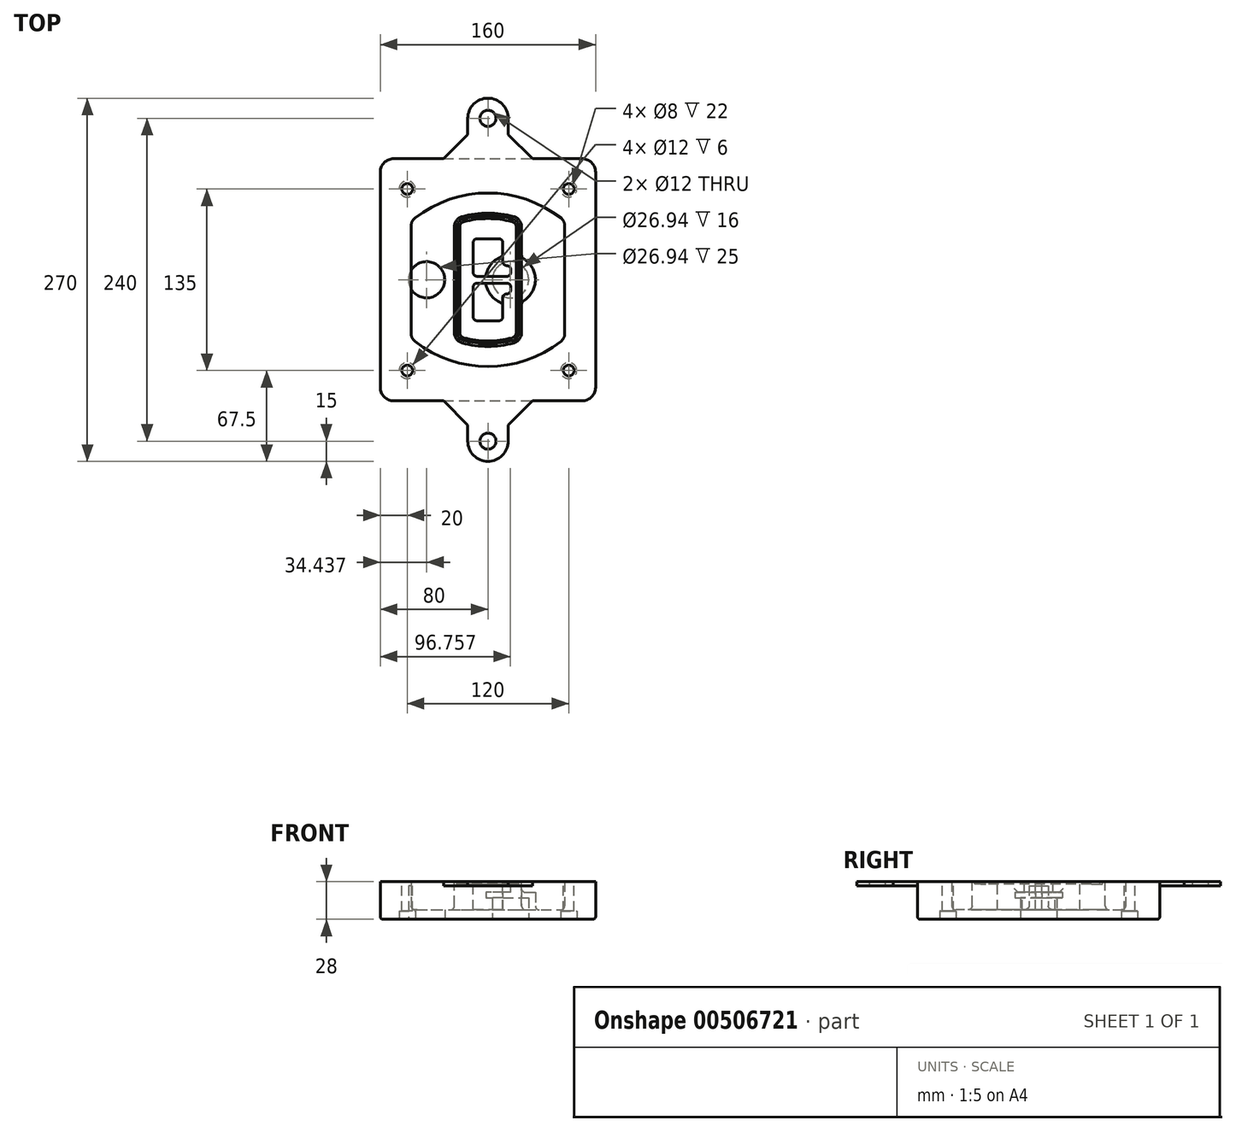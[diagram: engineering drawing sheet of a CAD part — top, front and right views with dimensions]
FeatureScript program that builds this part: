
annotation { "Feature Type Name" : "Feature", "Feature Type Description" : "" }
export const myFeature = defineFeature(function(context is Context, id is Id, definition is map)
    precondition{}
    {
        {
            var Q0;
            Q0=qCreatedBy(makeId("Top.planeOp"),FACE);
            var sketch = newSketch(context, id + "F0", { "sketchPlane" : qUnion([Q0])});
            skPoint(sketch, "E0.rect.middle", {"position": v(0, 0) * mm});
            skLineSegment(sketch, "E1.bottom", {"start": v(-70, -90) * mm, "end": v(70, -90) * mm});
            skLineSegment(sketch, "E1.top", {"start": v(-70, 90) * mm, "end": v(70, 90) * mm});
            skLineSegment(sketch, "E1.left", {"start": v(-80, -80) * mm, "end": v(-80, 80) * mm});
            skLineSegment(sketch, "E1.right", {"start": v(80, -80) * mm, "end": v(80, 80) * mm});
            skLineSegment(sketch, "E2", {"start": v(-80, 90) * mm, "end": v(80, -90) * mm, "construction": true});
            skLineSegment(sketch, "E3", {"start": v(80, 90) * mm, "end": v(-80, -90) * mm, "construction": true});
            skCircle(sketch, "E4", {"center": v(-60, 67.5) * mm, "radius": 4 * mm});
            skCircle(sketch, "E5", {"center": v(60, 67.5) * mm, "radius": 4 * mm});
            skCircle(sketch, "E6", {"center": v(60, -67.5) * mm, "radius": 4 * mm});
            skCircle(sketch, "E7", {"center": v(-60, -67.5) * mm, "radius": 4 * mm});
            skLineSegment(sketch, "E8", {"start": v(-60, 67.5) * mm, "end": v(60, 67.5) * mm, "construction": true});
            skLineSegment(sketch, "E9", {"start": v(60, 67.5) * mm, "end": v(60, -67.5) * mm, "construction": true});
            skLineSegment(sketch, "E10", {"start": v(60, -67.5) * mm, "end": v(-60, -67.5) * mm, "construction": true});
            skLineSegment(sketch, "E11", {"start": v(-60, -67.5) * mm, "end": v(-60, 67.5) * mm, "construction": true});
            skLineSegment(sketch, "E12", {"start": v(-60, 40.3) * mm, "end": v(-60, -40.3) * mm});
            skLineSegment(sketch, "E13", {"start": v(60, 40.3) * mm, "end": v(60, -40.3) * mm});
            skArc(sketch, "E14", {"start": v(56.15, 48.18) * mm, "mid": v(0, 67.5) * mm, "end": v(-56.15, 48.18) * mm});
            skArc(sketch, "E15", {"start": v(-56.15, -48.18) * mm, "mid": v(0, -67.5) * mm, "end": v(56.15, -48.18) * mm});
            skLineSegment(sketch, "E16", {"start": v(-60, 0) * mm, "end": v(60, 0) * mm, "construction": true});
            skPoint(sketch, "E17.visualSharp", {"position": v(-60, -45) * mm});
            skArc(sketch, "E17.filletArc", {"start": v(-60, -40.3) * mm, "mid": v(-58.99, -44.68) * mm, "end": v(-56.15, -48.18) * mm});
            skPoint(sketch, "E18.visualSharp", {"position": v(-60, 45) * mm});
            skArc(sketch, "E18.filletArc", {"start": v(-56.15, 48.18) * mm, "mid": v(-58.99, 44.68) * mm, "end": v(-60, 40.3) * mm});
            skPoint(sketch, "E19.visualSharp", {"position": v(60, 45) * mm});
            skArc(sketch, "E19.filletArc", {"start": v(60, 40.3) * mm, "mid": v(58.99, 44.68) * mm, "end": v(56.15, 48.18) * mm});
            skPoint(sketch, "E20.visualSharp", {"position": v(60, -45) * mm});
            skArc(sketch, "E20.filletArc", {"start": v(56.15, -48.18) * mm, "mid": v(58.99, -44.68) * mm, "end": v(60, -40.3) * mm});
            skPoint(sketch, "E21.visualSharp", {"position": v(-80, 90) * mm});
            skArc(sketch, "E21.filletArc", {"start": v(-70, 90) * mm, "mid": v(-77.07, 87.07) * mm, "end": v(-80, 80) * mm});
            skPoint(sketch, "E22.visualSharp", {"position": v(80, 90) * mm});
            skArc(sketch, "E22.filletArc", {"start": v(80, 80) * mm, "mid": v(77.07, 87.07) * mm, "end": v(70, 90) * mm});
            skPoint(sketch, "E23.visualSharp", {"position": v(80, -90) * mm});
            skArc(sketch, "E23.filletArc", {"start": v(70, -90) * mm, "mid": v(77.07, -87.07) * mm, "end": v(80, -80) * mm});
            skPoint(sketch, "E24.visualSharp", {"position": v(-80, -90) * mm});
            skArc(sketch, "E24.filletArc", {"start": v(-80, -80) * mm, "mid": v(-77.07, -87.07) * mm, "end": v(-70, -90) * mm});
            skArc(sketch, "E25.0", {"start": v(57, 40.3) * mm, "mid": v(56.3, 43.36) * mm, "end": v(54.3, 45.81) * mm});
            skLineSegment(sketch, "E25.1", {"start": v(57, 40.3) * mm, "end": v(57, -40.3) * mm});
            skArc(sketch, "E25.2", {"start": v(54.3, -45.81) * mm, "mid": v(56.3, -43.36) * mm, "end": v(57, -40.3) * mm});
            skArc(sketch, "E25.3", {"start": v(-54.3, -45.81) * mm, "mid": v(0, -64.5) * mm, "end": v(54.3, -45.81) * mm});
            skArc(sketch, "E25.4", {"start": v(-57, -40.3) * mm, "mid": v(-56.3, -43.36) * mm, "end": v(-54.3, -45.81) * mm});
            skArc(sketch, "E25.5", {"start": v(54.3, 45.81) * mm, "mid": v(0, 64.5) * mm, "end": v(-54.3, 45.81) * mm});
            skLineSegment(sketch, "E25.6", {"start": v(-57, 40.3) * mm, "end": v(-57, -40.3) * mm});
            skArc(sketch, "E25.7", {"start": v(-54.3, 45.81) * mm, "mid": v(-56.3, 43.36) * mm, "end": v(-57, 40.3) * mm});
            skArc(sketch, "E26.0", {"start": v(-58.62, 51.33) * mm, "mid": v(-62.58, 46.43) * mm, "end": v(-64, 40.3) * mm});
            skArc(sketch, "E26.1", {"start": v(58.62, 51.33) * mm, "mid": v(0, 71.5) * mm, "end": v(-58.62, 51.33) * mm});
            skArc(sketch, "E26.2", {"start": v(64, 40.3) * mm, "mid": v(62.58, 46.43) * mm, "end": v(58.62, 51.33) * mm});
            skLineSegment(sketch, "E26.3", {"start": v(64, 40.3) * mm, "end": v(64, -40.3) * mm});
            skArc(sketch, "E26.4", {"start": v(58.62, -51.33) * mm, "mid": v(62.58, -46.43) * mm, "end": v(64, -40.3) * mm});
            skLineSegment(sketch, "E26.5", {"start": v(-64, 40.3) * mm, "end": v(-64, -40.3) * mm});
            skArc(sketch, "E26.6", {"start": v(-58.62, -51.33) * mm, "mid": v(0, -71.5) * mm, "end": v(58.62, -51.33) * mm});
            skArc(sketch, "E26.7", {"start": v(-64, -40.3) * mm, "mid": v(-62.58, -46.43) * mm, "end": v(-58.62, -51.33) * mm});
            skSolve(sketch);
        }
        {
            var Q0;
            Q0=makeQuery(id+"F0.imprint","IMPRINT",FACE,{"disambiguationData":[TD([[makeQuery(id+"F0.imprint","IMPRINT",EDGE,{"derivedFrom":sQuery(id+"F0.wireOp",EDGE,"E1.bottom")}),1.0]])]});
            var Q1;
            Q1=makeQuery(id+"F0.imprint","IMPRINT",FACE,{"disambiguationData":[TD([[makeQuery(id+"F0.imprint","IMPRINT",EDGE,{"derivedFrom":sQuery(id+"F0.wireOp",EDGE,"E12")}),1.0]])]});
            var Q2;
            Q2=makeQuery(id+"F0.imprint","IMPRINT",FACE,{"disambiguationData":[TD([[makeQuery(id+"F0.imprint","IMPRINT",EDGE,{"derivedFrom":sQuery(id+"F0.wireOp",EDGE,"E25.0")}),1.0]])]});
            var Q3;
            Q3=makeQuery(id+"F0.imprint","IMPRINT",FACE,{"disambiguationData":[TD([[makeQuery(id+"F0.imprint","IMPRINT",EDGE,{"derivedFrom":sQuery(id+"F0.wireOp",EDGE,"E12")}),-1.0]])]});
            extrude(context, id + "F1", {"entities" : qUnion([Q0, Q1, Q2, Q3]), "oppositeDirection" : true, "depth" : 25 * mm});
        }
        {
            var Q0;
            Q0=makeQuery(id+"F0.imprint","IMPRINT",FACE,{"disambiguationData":[TD([[makeQuery(id+"F0.imprint","IMPRINT",EDGE,{"derivedFrom":sQuery(id+"F0.wireOp",EDGE,"E12")}),1.0]])]});
            extrude(context, id + "F2", {"entities" : qUnion([Q0]), "operationType" : NewBodyOperationType.ADD, "depth" : 3 * mm});
        }
        {
            var Q0;
            Q0=makeQuery(id+"F0.imprint","IMPRINT",FACE,{"disambiguationData":[TD([[makeQuery(id+"F0.imprint","IMPRINT",EDGE,{"derivedFrom":sQuery(id+"F0.wireOp",EDGE,"E25.0")}),1.0]])]});
            extrude(context, id + "F3", {"entities" : qUnion([Q0]), "operationType" : NewBodyOperationType.REMOVE, "oppositeDirection" : true, "depth" : 18 * mm});
        }
        {
            var Q0;
            Q0=makeQuery(id+"F2.opExtrude","CAP_FACE",FACE,{"disambiguationData":[OSD([sQuery(id+"F0.wireOp",EDGE,"E12"),sQuery(id+"F0.wireOp",EDGE,"E13"),sQuery(id+"F0.wireOp",EDGE,"E14"),sQuery(id+"F0.wireOp",EDGE,"E15"),sQuery(id+"F0.wireOp",EDGE,"E17.filletArc"),sQuery(id+"F0.wireOp",EDGE,"E18.filletArc"),sQuery(id+"F0.wireOp",EDGE,"E19.filletArc"),sQuery(id+"F0.wireOp",EDGE,"E20.filletArc"),sQuery(id+"F0.wireOp",EDGE,"E25.0"),sQuery(id+"F0.wireOp",EDGE,"E25.1"),sQuery(id+"F0.wireOp",EDGE,"E25.2"),sQuery(id+"F0.wireOp",EDGE,"E25.3"),sQuery(id+"F0.wireOp",EDGE,"E25.4"),sQuery(id+"F0.wireOp",EDGE,"E25.5"),sQuery(id+"F0.wireOp",EDGE,"E25.6"),sQuery(id+"F0.wireOp",EDGE,"E25.7")])],"isStart":false});
            var sketch = newSketch(context, id + "F4", { "sketchPlane" : qUnion([Q0])});
            skArc(sketch, "E27.0", {"start": v(-19.08, -46.97) * mm, "mid": v(0, -49.5) * mm, "end": v(19.08, -46.97) * mm});
            skArc(sketch, "E28.0", {"start": v(19.08, 46.97) * mm, "mid": v(0, 49.5) * mm, "end": v(-19.08, 46.97) * mm});
            skLineSegment(sketch, "E29", {"start": v(-25, 39.25) * mm, "end": v(-25, -39.25) * mm});
            skLineSegment(sketch, "E30", {"start": v(25, 39.25) * mm, "end": v(25, -39.25) * mm});
            skLineSegment(sketch, "E31", {"start": v(-25, 45.1) * mm, "end": v(25, 45.1) * mm, "construction": true});
            skLineSegment(sketch, "E32", {"start": v(-25, -45.1) * mm, "end": v(25, -45.1) * mm, "construction": true});
            skPoint(sketch, "E33.visualSharp", {"position": v(-25, 45.1) * mm});
            skArc(sketch, "E33.filletArc", {"start": v(-19.08, 46.97) * mm, "mid": v(-23.35, 44.11) * mm, "end": v(-25, 39.25) * mm});
            skPoint(sketch, "E34.visualSharp", {"position": v(25, 45.1) * mm});
            skArc(sketch, "E34.filletArc", {"start": v(25, 39.25) * mm, "mid": v(23.35, 44.11) * mm, "end": v(19.08, 46.97) * mm});
            skPoint(sketch, "E35.visualSharp", {"position": v(25, -45.1) * mm});
            skArc(sketch, "E35.filletArc", {"start": v(19.08, -46.97) * mm, "mid": v(23.35, -44.11) * mm, "end": v(25, -39.25) * mm});
            skPoint(sketch, "E36.visualSharp", {"position": v(-25, -45.1) * mm});
            skArc(sketch, "E36.filletArc", {"start": v(-25, -39.25) * mm, "mid": v(-23.35, -44.11) * mm, "end": v(-19.08, -46.97) * mm});
            skArc(sketch, "E37.0", {"start": v(54.3, 45.81) * mm, "mid": v(0, 64.5) * mm, "end": v(-54.3, 45.81) * mm});
            skArc(sketch, "E37.1", {"start": v(-54.3, 45.81) * mm, "mid": v(-56.3, 43.36) * mm, "end": v(-57, 40.3) * mm});
            skLineSegment(sketch, "E37.2", {"start": v(-57, 40.3) * mm, "end": v(-57, -40.3) * mm});
            skArc(sketch, "E37.3", {"start": v(-57, -40.3) * mm, "mid": v(-56.3, -43.36) * mm, "end": v(-54.3, -45.81) * mm});
            skArc(sketch, "E37.4", {"start": v(-54.3, -45.81) * mm, "mid": v(0, -64.5) * mm, "end": v(54.3, -45.81) * mm});
            skArc(sketch, "E37.5", {"start": v(54.3, -45.81) * mm, "mid": v(56.3, -43.36) * mm, "end": v(57, -40.3) * mm});
            skLineSegment(sketch, "E37.6", {"start": v(57, 40.3) * mm, "end": v(57, -40.3) * mm});
            skArc(sketch, "E37.7", {"start": v(57, 40.3) * mm, "mid": v(56.3, 43.36) * mm, "end": v(54.3, 45.81) * mm});
            skLineSegment(sketch, "E38.0", {"start": v(23, 39.25) * mm, "end": v(23, -39.25) * mm});
            skArc(sketch, "E38.1", {"start": v(18.56, -45.04) * mm, "mid": v(21.76, -42.9) * mm, "end": v(23, -39.25) * mm});
            skArc(sketch, "E38.2", {"start": v(-18.56, -45.04) * mm, "mid": v(0, -47.5) * mm, "end": v(18.56, -45.04) * mm});
            skArc(sketch, "E38.3", {"start": v(-23, -39.25) * mm, "mid": v(-21.76, -42.9) * mm, "end": v(-18.56, -45.04) * mm});
            skLineSegment(sketch, "E38.4", {"start": v(-23, 39.25) * mm, "end": v(-23, -39.25) * mm});
            skArc(sketch, "E38.5", {"start": v(23, 39.25) * mm, "mid": v(21.76, 42.9) * mm, "end": v(18.56, 45.04) * mm});
            skArc(sketch, "E38.6", {"start": v(-18.56, 45.04) * mm, "mid": v(-21.76, 42.9) * mm, "end": v(-23, 39.25) * mm});
            skArc(sketch, "E38.7", {"start": v(18.56, 45.04) * mm, "mid": v(0, 47.5) * mm, "end": v(-18.56, 45.04) * mm});
            skArc(sketch, "E39.0", {"start": v(21, 39.25) * mm, "mid": v(20.18, 41.68) * mm, "end": v(18.04, 43.1) * mm});
            skLineSegment(sketch, "E39.1", {"start": v(21, 39.25) * mm, "end": v(21, -39.25) * mm});
            skArc(sketch, "E39.2", {"start": v(18.04, -43.1) * mm, "mid": v(20.18, -41.68) * mm, "end": v(21, -39.25) * mm});
            skArc(sketch, "E39.3", {"start": v(-18.04, -43.1) * mm, "mid": v(0, -45.5) * mm, "end": v(18.04, -43.1) * mm});
            skArc(sketch, "E39.4", {"start": v(-21, -39.25) * mm, "mid": v(-20.18, -41.68) * mm, "end": v(-18.04, -43.1) * mm});
            skArc(sketch, "E39.5", {"start": v(18.04, 43.1) * mm, "mid": v(0, 45.5) * mm, "end": v(-18.04, 43.1) * mm});
            skLineSegment(sketch, "E39.6", {"start": v(-21, 39.25) * mm, "end": v(-21, -39.25) * mm});
            skArc(sketch, "E39.7", {"start": v(-18.04, 43.1) * mm, "mid": v(-20.18, 41.68) * mm, "end": v(-21, 39.25) * mm});
            skLineSegment(sketch, "E40", {"start": v(-25, 0) * mm, "end": v(25, 0) * mm, "construction": true});
            skLineSegment(sketch, "E41", {"start": v(-11, 5.5) * mm, "end": v(-11, 27.5) * mm});
            skLineSegment(sketch, "E42", {"start": v(-8, 30.5) * mm, "end": v(8, 30.5) * mm});
            skLineSegment(sketch, "E43", {"start": v(11, 27.5) * mm, "end": v(11, 13.5) * mm});
            skLineSegment(sketch, "E44", {"start": v(14, 10.5) * mm, "end": v(14, 10.5) * mm});
            skLineSegment(sketch, "E45", {"start": v(17, 7.5) * mm, "end": v(17, 5.5) * mm});
            skLineSegment(sketch, "E46", {"start": v(14, 2.5) * mm, "end": v(-8, 2.5) * mm});
            skPoint(sketch, "E47.visualSharp", {"position": v(-11, 30.5) * mm});
            skArc(sketch, "E47.filletArc", {"start": v(-8, 30.5) * mm, "mid": v(-10.12, 29.62) * mm, "end": v(-11, 27.5) * mm});
            skPoint(sketch, "E48.visualSharp", {"position": v(11, 30.5) * mm});
            skArc(sketch, "E48.filletArc", {"start": v(11, 27.5) * mm, "mid": v(10.12, 29.62) * mm, "end": v(8, 30.5) * mm});
            skPoint(sketch, "E49.visualSharp", {"position": v(11, 10.5) * mm});
            skArc(sketch, "E49.filletArc", {"start": v(11, 13.5) * mm, "mid": v(11.88, 11.38) * mm, "end": v(14, 10.5) * mm});
            skPoint(sketch, "E50.visualSharp", {"position": v(17, 10.5) * mm});
            skArc(sketch, "E50.filletArc", {"start": v(17, 7.5) * mm, "mid": v(16.12, 9.62) * mm, "end": v(14, 10.5) * mm});
            skPoint(sketch, "E51.visualSharp", {"position": v(17, 2.5) * mm});
            skArc(sketch, "E51.filletArc", {"start": v(14, 2.5) * mm, "mid": v(16.12, 3.38) * mm, "end": v(17, 5.5) * mm});
            skPoint(sketch, "E52.visualSharp", {"position": v(-11, 2.5) * mm});
            skArc(sketch, "E52.filletArc", {"start": v(-11, 5.5) * mm, "mid": v(-10.12, 3.38) * mm, "end": v(-8, 2.5) * mm});
            skLineSegment(sketch, "E53.0.MirrorCS", {"start": v(14, -2.5) * mm, "end": v(-8, -2.5) * mm});
            skArc(sketch, "E54.0.MirrorCS", {"start": v(-11, -5.5) * mm, "mid": v(-10.12, -3.38) * mm, "end": v(-8, -2.5) * mm});
            skLineSegment(sketch, "E55.0.MirrorCS", {"start": v(-11, -5.5) * mm, "end": v(-11, -27.5) * mm});
            skArc(sketch, "E56.0.MirrorCS", {"start": v(-8, -30.5) * mm, "mid": v(-10.12, -29.62) * mm, "end": v(-11, -27.5) * mm});
            skLineSegment(sketch, "E57.0.MirrorCS", {"start": v(-8, -30.5) * mm, "end": v(8, -30.5) * mm});
            skArc(sketch, "E58.0.MirrorCS", {"start": v(11, -27.5) * mm, "mid": v(10.12, -29.62) * mm, "end": v(8, -30.5) * mm});
            skLineSegment(sketch, "E59.0.MirrorCS", {"start": v(11, -27.5) * mm, "end": v(11, -13.5) * mm});
            skArc(sketch, "E60.0.MirrorCS", {"start": v(11, -13.5) * mm, "mid": v(11.88, -11.38) * mm, "end": v(14, -10.5) * mm});
            skArc(sketch, "E61.0.MirrorCS", {"start": v(17, -7.5) * mm, "mid": v(16.12, -9.62) * mm, "end": v(14, -10.5) * mm});
            skLineSegment(sketch, "E62.0.MirrorCS", {"start": v(17, -7.5) * mm, "end": v(17, -5.5) * mm});
            skArc(sketch, "E63.0.MirrorCS", {"start": v(14, -2.5) * mm, "mid": v(16.12, -3.38) * mm, "end": v(17, -5.5) * mm});
            skSolve(sketch);
        }
        {
            var Q0;
            Q0=makeQuery(id+"F4.imprint","IMPRINT",FACE,{"disambiguationData":[TD([[makeQuery(id+"F4.imprint","IMPRINT",EDGE,{"derivedFrom":sQuery(id+"F4.wireOp",EDGE,"E27.0")}),1.0]])]});
            var Q1;
            Q1=makeQuery(id+"F4.imprint","IMPRINT",FACE,{"disambiguationData":[TD([[makeQuery(id+"F4.imprint","IMPRINT",EDGE,{"derivedFrom":sQuery(id+"F4.wireOp",EDGE,"E38.0")}),-1.0]])]});
            var Q2;
            Q2=makeQuery(id+"F4.imprint","IMPRINT",FACE,{"disambiguationData":[TD([[makeQuery(id+"F4.imprint","IMPRINT",EDGE,{"derivedFrom":sQuery(id+"F4.wireOp",EDGE,"E39.0")}),1.0]])]});
            extrude(context, id + "F5", {"entities" : qUnion([Q0, Q1, Q2]), "operationType" : NewBodyOperationType.ADD, "endBound" : BoundingType.UP_TO_NEXT, "oppositeDirection" : true, "depth" : 25 * mm});
        }
        {
            var Q0;
            Q0=makeQuery(id+"F4.imprint","IMPRINT",FACE,{"disambiguationData":[TD([[makeQuery(id+"F4.imprint","IMPRINT",EDGE,{"derivedFrom":sQuery(id+"F4.wireOp",EDGE,"E38.0")}),-1.0]])]});
            extrude(context, id + "F6", {"entities" : qUnion([Q0]), "operationType" : NewBodyOperationType.REMOVE, "oppositeDirection" : true, "depth" : 2 * mm});
        }
        {
            var Q0;
            Q0=makeQuery(id+"F1.opExtrude","CAP_FACE",FACE,{"disambiguationData":[OSD([sQuery(id+"F0.wireOp",EDGE,"E1.bottom"),sQuery(id+"F0.wireOp",EDGE,"E1.top"),sQuery(id+"F0.wireOp",EDGE,"E1.left"),sQuery(id+"F0.wireOp",EDGE,"E1.right"),sQuery(id+"F0.wireOp",EDGE,"E4"),sQuery(id+"F0.wireOp",EDGE,"E5"),sQuery(id+"F0.wireOp",EDGE,"E6"),sQuery(id+"F0.wireOp",EDGE,"E7"),sQuery(id+"F0.wireOp",EDGE,"E21.filletArc"),sQuery(id+"F0.wireOp",EDGE,"E22.filletArc"),sQuery(id+"F0.wireOp",EDGE,"E23.filletArc"),sQuery(id+"F0.wireOp",EDGE,"E24.filletArc")])],"isStart":false});
            var sketch = newSketch(context, id + "F7", { "sketchPlane" : qUnion([Q0])});
            skCircle(sketch, "E64", {"center": v(16.76, 0) * mm, "radius": 13.47 * mm});
            skCircle(sketch, "E65", {"center": v(-45.56, 0) * mm, "radius": 13.47 * mm});
            skLineSegment(sketch, "E66", {"start": v(80, 0) * mm, "end": v(-80, 0) * mm});
            skCircle(sketch, "E67", {"center": v(16.76, 0) * mm, "radius": 18.47 * mm});
            skCircle(sketch, "E68", {"center": v(60, -67.5) * mm, "radius": 6 * mm});
            skCircle(sketch, "E69", {"center": v(-60, -67.5) * mm, "radius": 6 * mm});
            skCircle(sketch, "E70", {"center": v(-60, 67.5) * mm, "radius": 6 * mm});
            skCircle(sketch, "E71", {"center": v(60, 67.5) * mm, "radius": 6 * mm});
            skSolve(sketch);
        }
        {
            var Q0;
            {var subQ1=sQuery(id+"F7.wireOp",EDGE,"E66");var subQ4=sQuery(id+"F7.wireOp",EDGE,"E64");var subQ6=makeQuery(id+"F7.imprint","INTERSECT",VERTEX,{"disambiguationData":[OD(0.0)],"derivedFrom":[subQ4,subQ1]});Q0=makeQuery(id+"F7.imprint","IMPRINT",FACE,{"disambiguationData":[TD([[makeQuery(id+"F7.imprint","IMPRINT",EDGE,{"disambiguationData":[TD([[subQ6,-1.0]])],"derivedFrom":subQ4}),-1.0]])]});}
            var Q1;
            {var subQ0=sQuery(id+"F7.wireOp",EDGE,"E66");var subQ1=sQuery(id+"F7.wireOp",EDGE,"E64");var subQ3=makeQuery(id+"F7.imprint","INTERSECT",VERTEX,{"disambiguationData":[OD(0.0)],"derivedFrom":[subQ1,subQ0]});Q1=makeQuery(id+"F7.imprint","IMPRINT",FACE,{"disambiguationData":[TD([[makeQuery(id+"F7.imprint","IMPRINT",EDGE,{"disambiguationData":[TD([[subQ3,-1.0]])],"derivedFrom":subQ1}),1.0]])]});}
            var Q2;
            {var subQ0=sQuery(id+"F7.wireOp",EDGE,"E66");var subQ1=sQuery(id+"F7.wireOp",EDGE,"E64");var subQ3=makeQuery(id+"F7.imprint","INTERSECT",VERTEX,{"disambiguationData":[OD(0.0)],"derivedFrom":[subQ1,subQ0]});Q2=makeQuery(id+"F7.imprint","IMPRINT",FACE,{"disambiguationData":[TD([[makeQuery(id+"F7.imprint","IMPRINT",EDGE,{"disambiguationData":[TD([[subQ3,1.0]])],"derivedFrom":subQ1}),1.0]])]});}
            var Q3;
            {var subQ1=sQuery(id+"F7.wireOp",EDGE,"E66");var subQ4=sQuery(id+"F7.wireOp",EDGE,"E64");var subQ6=makeQuery(id+"F7.imprint","INTERSECT",VERTEX,{"disambiguationData":[OD(0.0)],"derivedFrom":[subQ4,subQ1]});Q3=makeQuery(id+"F7.imprint","IMPRINT",FACE,{"disambiguationData":[TD([[makeQuery(id+"F7.imprint","IMPRINT",EDGE,{"disambiguationData":[TD([[subQ6,1.0]])],"derivedFrom":subQ4}),-1.0]])]});}
            extrude(context, id + "F8", {"entities" : qUnion([Q0, Q1, Q2, Q3]), "operationType" : NewBodyOperationType.ADD, "oppositeDirection" : true, "depth" : 20 * mm});
        }
        {
            var Q0;
            {var subQ0=sQuery(id+"F7.wireOp",EDGE,"E66");var subQ1=sQuery(id+"F7.wireOp",EDGE,"E64");var subQ3=makeQuery(id+"F7.imprint","INTERSECT",VERTEX,{"disambiguationData":[OD(0.0)],"derivedFrom":[subQ1,subQ0]});Q0=makeQuery(id+"F7.imprint","IMPRINT",FACE,{"disambiguationData":[TD([[makeQuery(id+"F7.imprint","IMPRINT",EDGE,{"disambiguationData":[TD([[subQ3,-1.0]])],"derivedFrom":subQ1}),1.0]])]});}
            var Q1;
            {var subQ0=sQuery(id+"F7.wireOp",EDGE,"E66");var subQ1=sQuery(id+"F7.wireOp",EDGE,"E64");var subQ3=makeQuery(id+"F7.imprint","INTERSECT",VERTEX,{"disambiguationData":[OD(0.0)],"derivedFrom":[subQ1,subQ0]});Q1=makeQuery(id+"F7.imprint","IMPRINT",FACE,{"disambiguationData":[TD([[makeQuery(id+"F7.imprint","IMPRINT",EDGE,{"disambiguationData":[TD([[subQ3,1.0]])],"derivedFrom":subQ1}),1.0]])]});}
            extrude(context, id + "F9", {"entities" : qUnion([Q0, Q1]), "operationType" : NewBodyOperationType.REMOVE, "oppositeDirection" : true, "depth" : 16 * mm});
        }
        {
            var Q0;
            {var subQ0=sQuery(id+"F7.wireOp",EDGE,"E66");var subQ1=sQuery(id+"F7.wireOp",EDGE,"E65");var subQ3=makeQuery(id+"F7.imprint","INTERSECT",VERTEX,{"disambiguationData":[OD(0.0)],"derivedFrom":[subQ1,subQ0]});Q0=makeQuery(id+"F7.imprint","IMPRINT",FACE,{"disambiguationData":[TD([[makeQuery(id+"F7.imprint","IMPRINT",EDGE,{"disambiguationData":[TD([[subQ3,-1.0]])],"derivedFrom":subQ1}),1.0]])]});}
            var Q1;
            {var subQ0=sQuery(id+"F7.wireOp",EDGE,"E66");var subQ1=sQuery(id+"F7.wireOp",EDGE,"E65");var subQ3=makeQuery(id+"F7.imprint","INTERSECT",VERTEX,{"disambiguationData":[OD(0.0)],"derivedFrom":[subQ1,subQ0]});Q1=makeQuery(id+"F7.imprint","IMPRINT",FACE,{"disambiguationData":[TD([[makeQuery(id+"F7.imprint","IMPRINT",EDGE,{"disambiguationData":[TD([[subQ3,1.0]])],"derivedFrom":subQ1}),1.0]])]});}
            extrude(context, id + "F10", {"entities" : qUnion([Q0, Q1]), "operationType" : NewBodyOperationType.REMOVE, "oppositeDirection" : true, "depth" : 25 * mm});
        }
        {
            var Q0;
            Q0=makeQuery(id+"F7.imprint","IMPRINT",FACE,{"disambiguationData":[TD([[makeQuery(id+"F7.imprint","IMPRINT",EDGE,{"derivedFrom":sQuery(id+"F7.wireOp",EDGE,"E68")}),1.0]])]});
            var Q1;
            Q1=makeQuery(id+"F7.imprint","IMPRINT",FACE,{"disambiguationData":[TD([[makeQuery(id+"F7.imprint","IMPRINT",EDGE,{"derivedFrom":makeQuery(id+"F1.opExtrude","CAP_EDGE",EDGE,{"disambiguationData":[OSD([sQuery(id+"F0.wireOp",EDGE,"E5")])],"isStart":false})}),-1.0]])]});
            var Q2;
            Q2=makeQuery(id+"F7.imprint","IMPRINT",FACE,{"disambiguationData":[TD([[makeQuery(id+"F7.imprint","IMPRINT",EDGE,{"derivedFrom":sQuery(id+"F7.wireOp",EDGE,"E69")}),1.0]])]});
            var Q3;
            Q3=makeQuery(id+"F7.imprint","IMPRINT",FACE,{"disambiguationData":[TD([[makeQuery(id+"F7.imprint","IMPRINT",EDGE,{"derivedFrom":makeQuery(id+"F1.opExtrude","CAP_EDGE",EDGE,{"disambiguationData":[OSD([sQuery(id+"F0.wireOp",EDGE,"E4")])],"isStart":false})}),-1.0]])]});
            var Q4;
            Q4=makeQuery(id+"F7.imprint","IMPRINT",FACE,{"disambiguationData":[TD([[makeQuery(id+"F7.imprint","IMPRINT",EDGE,{"derivedFrom":sQuery(id+"F7.wireOp",EDGE,"E70")}),1.0]])]});
            var Q5;
            Q5=makeQuery(id+"F7.imprint","IMPRINT",FACE,{"disambiguationData":[TD([[makeQuery(id+"F7.imprint","IMPRINT",EDGE,{"derivedFrom":makeQuery(id+"F1.opExtrude","CAP_EDGE",EDGE,{"disambiguationData":[OSD([sQuery(id+"F0.wireOp",EDGE,"E7")])],"isStart":false})}),-1.0]])]});
            var Q6;
            Q6=makeQuery(id+"F7.imprint","IMPRINT",FACE,{"disambiguationData":[TD([[makeQuery(id+"F7.imprint","IMPRINT",EDGE,{"derivedFrom":sQuery(id+"F7.wireOp",EDGE,"E71")}),1.0]])]});
            var Q7;
            Q7=makeQuery(id+"F7.imprint","IMPRINT",FACE,{"disambiguationData":[TD([[makeQuery(id+"F7.imprint","IMPRINT",EDGE,{"derivedFrom":makeQuery(id+"F1.opExtrude","CAP_EDGE",EDGE,{"disambiguationData":[OSD([sQuery(id+"F0.wireOp",EDGE,"E6")])],"isStart":false})}),-1.0]])]});
            extrude(context, id + "F11", {"entities" : qUnion([Q0, Q1, Q2, Q3, Q4, Q5, Q6, Q7]), "operationType" : NewBodyOperationType.REMOVE, "oppositeDirection" : true, "depth" : 6 * mm});
        }
        {
            var Q0;
            Q0=makeQuery(id+"F9.boolean.opBoolean","COPY",FACE,{"derivedFrom":makeQuery(id+"F9.opExtrude","CAP_FACE",FACE,{"disambiguationData":[OSD([sQuery(id+"F7.wireOp",EDGE,"E64")])],"isStart":false})});
            var sketch = newSketch(context, id + "F12", { "sketchPlane" : qUnion([Q0])});
            skArc(sketch, "E72.0", {"start": v(11, 17.55) * mm, "mid": v(2.57, 11.82) * mm, "end": v(-1.54, 2.5) * mm});
            skArc(sketch, "E72.1", {"start": v(-1.54, -2.5) * mm, "mid": v(2.57, -11.82) * mm, "end": v(11, -17.55) * mm});
            skLineSegment(sketch, "E73", {"start": v(-1.54, -2.5) * mm, "end": v(14, -2.5) * mm});
            skLineSegment(sketch, "E74.0", {"start": v(14, 2.5) * mm, "end": v(-1.54, 2.5) * mm});
            skArc(sketch, "E74.1", {"start": v(14, 2.5) * mm, "mid": v(16.12, 3.38) * mm, "end": v(17, 5.5) * mm});
            skLineSegment(sketch, "E74.2", {"start": v(17, 7.5) * mm, "end": v(17, 5.5) * mm});
            skArc(sketch, "E74.3", {"start": v(17, 7.5) * mm, "mid": v(16.12, 9.62) * mm, "end": v(14, 10.5) * mm});
            skArc(sketch, "E74.4", {"start": v(11, 13.5) * mm, "mid": v(11.88, 11.38) * mm, "end": v(14, 10.5) * mm});
            skLineSegment(sketch, "E74.5", {"start": v(11, 17.55) * mm, "end": v(11, 13.5) * mm});
            skLineSegment(sketch, "E74.7", {"start": v(14, -2.5) * mm, "end": v(-1.54, -2.5) * mm});
            skArc(sketch, "E74.8", {"start": v(14, -2.5) * mm, "mid": v(16.12, -3.38) * mm, "end": v(17, -5.5) * mm});
            skLineSegment(sketch, "E74.9", {"start": v(17, -7.5) * mm, "end": v(17, -5.5) * mm});
            skArc(sketch, "E74.10", {"start": v(17, -7.5) * mm, "mid": v(16.12, -9.62) * mm, "end": v(14, -10.5) * mm});
            skArc(sketch, "E74.11", {"start": v(11, -13.5) * mm, "mid": v(11.88, -11.38) * mm, "end": v(14, -10.5) * mm});
            skLineSegment(sketch, "E74.12", {"start": v(11, -17.55) * mm, "end": v(11, -13.5) * mm});
            skPoint(sketch, "E75.orphan", {"position": v(11, -27.5) * mm});
            skPoint(sketch, "E76.orphan", {"position": v(-8, -2.5) * mm});
            skPoint(sketch, "E77.orphan", {"position": v(-8, 2.5) * mm});
            skPoint(sketch, "E78.orphan", {"position": v(11, 27.5) * mm});
            skSolve(sketch);
        }
        {
            var Q0;
            {var subQ7=sQuery(id+"F12.wireOp",EDGE,"E72.0");var subQ14=sQuery(id+"F12.wireOp",EDGE,"E72.1");var subQ16=sQuery(id+"F12.wireOp",EDGE,"E74.1");var subQ18=sQuery(id+"F12.wireOp",EDGE,"E74.8");Q0=qUnion([makeQuery(id+"F12.imprint","IMPRINT",FACE,{"disambiguationData":[TD([[makeQuery(id+"F12.imprint","IMPRINT",EDGE,{"derivedFrom":subQ7}),1.0]])]}),makeQuery(id+"F12.imprint","IMPRINT",FACE,{"disambiguationData":[TD([[makeQuery(id+"F12.imprint","IMPRINT",EDGE,{"derivedFrom":subQ14}),1.0]])]}),makeQuery(id+"F12.imprint","IMPRINT",FACE,{"disambiguationData":[TD([[makeQuery(id+"F12.imprint","IMPRINT",EDGE,{"derivedFrom":subQ16}),1.0]])]}),makeQuery(id+"F12.imprint","IMPRINT",FACE,{"disambiguationData":[TD([[makeQuery(id+"F12.imprint","IMPRINT",EDGE,{"derivedFrom":subQ18}),-1.0]])]})]);}
            var Q1;
            Q1=makeQuery(id+"F5.boolean.opBoolean","SPLIT",FACE,{"disambiguationData":[TD([makeQuery(id+"F5.opExtrude","SWEPT_FACE",FACE,{"disambiguationData":[OSD([sQuery(id+"F4.wireOp",EDGE,"E41")])]})])],"derivedFrom":makeQuery(id+"F3.boolean.opBoolean","COPY",FACE,{"derivedFrom":makeQuery(id+"F3.opExtrude","CAP_FACE",FACE,{"disambiguationData":[OSD([sQuery(id+"F0.wireOp",EDGE,"E25.0"),sQuery(id+"F0.wireOp",EDGE,"E25.1"),sQuery(id+"F0.wireOp",EDGE,"E25.2"),sQuery(id+"F0.wireOp",EDGE,"E25.3"),sQuery(id+"F0.wireOp",EDGE,"E25.4"),sQuery(id+"F0.wireOp",EDGE,"E25.5"),sQuery(id+"F0.wireOp",EDGE,"E25.6"),sQuery(id+"F0.wireOp",EDGE,"E25.7")])],"isStart":false})})});
            extrude(context, id + "F13", {"entities" : qUnion([Q0]), "operationType" : NewBodyOperationType.REMOVE, "endBound" : BoundingType.UP_TO_SURFACE, "endBoundEntityFace" : qUnion([Q1]), "depth" : 25 * mm});
        }
        {
            var Q0;
            Q0=makeQuery(id+"F3.boolean.opBoolean","COPY",EDGE,{"derivedFrom":makeQuery(id+"F3.opExtrude","CAP_EDGE",EDGE,{"disambiguationData":[OSD([sQuery(id+"F0.wireOp",EDGE,"E25.6")])],"isStart":false})});
            var Q1;
            Q1=makeQuery(id+"F8.boolean.opBoolean","INTERSECT",EDGE,{"derivedFrom":[makeQuery(id+"F5.opExtrude","SWEPT_FACE",FACE,{"disambiguationData":[OSD([sQuery(id+"F4.wireOp",EDGE,"E30")])]}),makeQuery(id+"F8.opExtrude","CAP_FACE",FACE,{"disambiguationData":[OSD([sQuery(id+"F7.wireOp",EDGE,"E67")])],"isStart":false})]});
            var Q2;
            Q2=makeQuery(id+"F8.boolean.opBoolean","INTERSECT",EDGE,{"disambiguationData":[OD(1.0)],"derivedFrom":[makeQuery(id+"F5.opExtrude","SWEPT_FACE",FACE,{"disambiguationData":[OSD([sQuery(id+"F4.wireOp",EDGE,"E30")])]}),makeQuery(id+"F8.opExtrude","SWEPT_FACE",FACE,{"disambiguationData":[OSD([sQuery(id+"F7.wireOp",EDGE,"E67")])]})]});
            var Q3;
            {var subQ0=sQuery(id+"F4.wireOp",EDGE,"E30");Q3=makeQuery(id+"F8.boolean.opBoolean","SPLIT",EDGE,{"disambiguationData":[TD([makeQuery(id+"F5.opExtrude","SWEPT_FACE",FACE,{"disambiguationData":[OSD([sQuery(id+"F4.wireOp",EDGE,"E35.filletArc")])]})])],"derivedFrom":makeQuery(id+"F5.opExtrude","CAP_EDGE",EDGE,{"disambiguationData":[OSD([subQ0])],"isStart":false})});}
            var Q4;
            {var subQ0=sQuery(id+"F0.wireOp",EDGE,"E25.7");var subQ1=sQuery(id+"F0.wireOp",EDGE,"E25.1");var subQ2=sQuery(id+"F0.wireOp",EDGE,"E25.6");var subQ3=sQuery(id+"F0.wireOp",EDGE,"E25.5");var subQ4=sQuery(id+"F0.wireOp",EDGE,"E25.4");var subQ5=sQuery(id+"F0.wireOp",EDGE,"E25.0");var subQ6=sQuery(id+"F0.wireOp",EDGE,"E25.2");var subQ7=sQuery(id+"F0.wireOp",EDGE,"E25.3");Q4=makeQuery(id+"F8.boolean.opBoolean","INTERSECT",EDGE,{"derivedFrom":[makeQuery(id+"F5.boolean.opBoolean","SPLIT",FACE,{"disambiguationData":[TD([makeQuery(id+"F2.opExtrude","SWEPT_FACE",FACE,{"disambiguationData":[OSD([subQ5])]})])],"derivedFrom":makeQuery(id+"F3.boolean.opBoolean","COPY",FACE,{"derivedFrom":makeQuery(id+"F3.opExtrude","CAP_FACE",FACE,{"disambiguationData":[OSD([subQ5,subQ1,subQ6,subQ7,subQ4,subQ3,subQ2,subQ0])],"isStart":false})})}),makeQuery(id+"F8.opExtrude","SWEPT_FACE",FACE,{"disambiguationData":[OSD([sQuery(id+"F7.wireOp",EDGE,"E67")])]})]});}
            var Q5;
            Q5=makeQuery(id+"F8.boolean.opBoolean","INTERSECT",EDGE,{"disambiguationData":[OD(0.0)],"derivedFrom":[makeQuery(id+"F5.opExtrude","SWEPT_FACE",FACE,{"disambiguationData":[OSD([sQuery(id+"F4.wireOp",EDGE,"E30")])]}),makeQuery(id+"F8.opExtrude","SWEPT_FACE",FACE,{"disambiguationData":[OSD([sQuery(id+"F7.wireOp",EDGE,"E67")])]})]});
            fillet(context, id + "F14", {"entities" : qUnion([Q0, Q1, Q2, Q3, Q4, Q5]), "radius" : 3 * mm, "tangentPropagation" : true, "allowEdgeOverflow" : false});
        }
        {
            var Q0;
            Q0=makeQuery(id+"F1.opExtrude","CAP_EDGE",EDGE,{"disambiguationData":[OSD([sQuery(id+"F0.wireOp",EDGE,"E1.bottom")])],"isStart":false});
            fillet(context, id + "F15", {"entities" : qUnion([Q0]), "radius" : 2 * mm, "tangentPropagation" : true, "allowEdgeOverflow" : false});
        }
        {
            var Q0;
            {var subQ0=sQuery(id+"F0.wireOp",EDGE,"E21.filletArc");var subQ1=sQuery(id+"F0.wireOp",EDGE,"E7");var subQ2=sQuery(id+"F0.wireOp",EDGE,"E6");var subQ3=sQuery(id+"F0.wireOp",EDGE,"E5");var subQ4=sQuery(id+"F0.wireOp",EDGE,"E4");var subQ5=sQuery(id+"F0.wireOp",EDGE,"E22.filletArc");var subQ6=sQuery(id+"F0.wireOp",EDGE,"E1.bottom");var subQ7=sQuery(id+"F0.wireOp",EDGE,"E1.right");var subQ8=sQuery(id+"F0.wireOp",EDGE,"E1.top");var subQ9=sQuery(id+"F0.wireOp",EDGE,"E1.left");var subQ10=sQuery(id+"F0.wireOp",EDGE,"E23.filletArc");var subQ11=sQuery(id+"F0.wireOp",EDGE,"E24.filletArc");Q0=makeQuery(id+"F2.boolean.opBoolean","SPLIT",FACE,{"disambiguationData":[TD([makeQuery(id+"F1.opExtrude","SWEPT_FACE",FACE,{"disambiguationData":[OSD([subQ6])]})])],"derivedFrom":makeQuery(id+"F1.opExtrude","CAP_FACE",FACE,{"disambiguationData":[OSD([subQ6,subQ8,subQ9,subQ7,subQ4,subQ3,subQ2,subQ1,subQ0,subQ5,subQ10,subQ11])],"isStart":true})});}
            var sketch = newSketch(context, id + "F16", { "sketchPlane" : qUnion([Q0])});
            skLineSegment(sketch, "E79", {"start": v(0, 120) * mm, "end": v(0, 90) * mm, "construction": true});
            skLineSegment(sketch, "E80", {"start": v(-33, 90) * mm, "end": v(-15, 108) * mm});
            skLineSegment(sketch, "E81", {"start": v(-15, 108) * mm, "end": v(-15, 120) * mm});
            skLineSegment(sketch, "E82", {"start": v(33, 90) * mm, "end": v(15, 108) * mm});
            skLineSegment(sketch, "E83", {"start": v(15, 108) * mm, "end": v(15, 120) * mm});
            skArc(sketch, "E84", {"start": v(15, 120) * mm, "mid": v(0, 135) * mm, "end": v(-15, 120) * mm});
            skCircle(sketch, "E85", {"center": v(0, 120) * mm, "radius": 6 * mm});
            skLineSegment(sketch, "E86", {"start": v(-80, 0) * mm, "end": v(80, 0) * mm, "construction": true});
            skLineSegment(sketch, "E87.MirrorCS", {"start": v(-33, -90) * mm, "end": v(-15, -108) * mm});
            skLineSegment(sketch, "E88.MirrorCS", {"start": v(-15, -108) * mm, "end": v(-15, -120) * mm});
            skArc(sketch, "E89.MirrorCS", {"start": v(15, -120) * mm, "mid": v(0, -135) * mm, "end": v(-15, -120) * mm});
            skCircle(sketch, "E90.MirrorC", {"center": v(0, -120) * mm, "radius": 6 * mm});
            skLineSegment(sketch, "E91.MirrorCS", {"start": v(0, -120) * mm, "end": v(0, -90) * mm, "construction": true});
            skLineSegment(sketch, "E92.MirrorCS", {"start": v(15, -108) * mm, "end": v(15, -120) * mm});
            skLineSegment(sketch, "E93.MirrorCS", {"start": v(33, -90) * mm, "end": v(15, -108) * mm});
            skSolve(sketch);
        }
        {
            var Q0;
            {var subQ1=sQuery(id+"F16.wireOp",EDGE,"E80");Q0=makeQuery(id+"F16.imprint","IMPRINT",FACE,{"disambiguationData":[TD([[makeQuery(id+"F16.imprint","IMPRINT",EDGE,{"derivedFrom":subQ1}),-1.0]])]});}
            var Q1;
            {var subQ0=sQuery(id+"F16.wireOp",EDGE,"E87.MirrorCS");Q1=makeQuery(id+"F16.imprint","IMPRINT",FACE,{"disambiguationData":[TD([[makeQuery(id+"F16.imprint","IMPRINT",EDGE,{"derivedFrom":subQ0}),1.0]])]});}
            var Q2;
            Q2=makeQuery(id+"F16.imprint","IMPRINT",FACE,{"disambiguationData":[TD([[makeQuery(id+"F16.imprint","IMPRINT",EDGE,{"derivedFrom":makeQuery(id+"F1.opExtrude","CAP_EDGE",EDGE,{"disambiguationData":[OSD([sQuery(id+"F0.wireOp",EDGE,"E1.left")])],"isStart":true})}),-1.0]])]});
            extrude(context, id + "F17", {"entities" : qUnion([Q0, Q1, Q2]), "operationType" : NewBodyOperationType.ADD, "depth" : 3 * mm});
        }
    });
